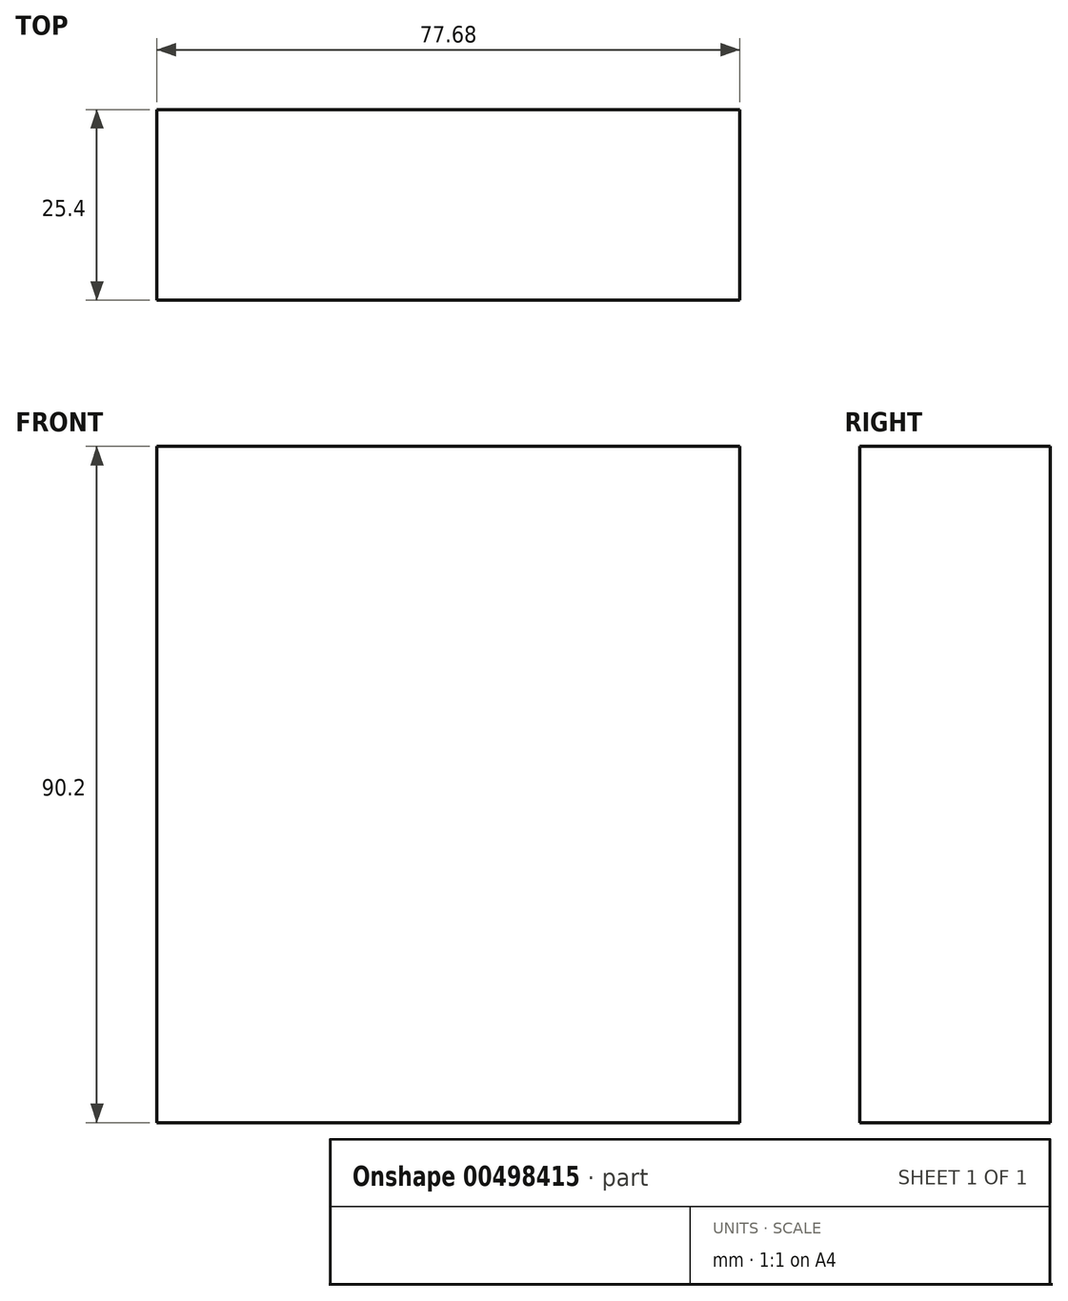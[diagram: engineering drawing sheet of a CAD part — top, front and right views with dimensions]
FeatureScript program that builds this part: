
annotation { "Feature Type Name" : "Feature", "Feature Type Description" : "" }
export const myFeature = defineFeature(function(context is Context, id is Id, definition is map)
    precondition{}
    {
        {
            var Q0;
            Q0=qCreatedBy(makeId("Front.planeOp"),FACE);
            var sketch = newSketch(context, id + "F0", { "sketchPlane" : qUnion([Q0])});
            skLineSegment(sketch, "E0.bottom", {"start": v(-33.07, 46.82) * mm, "end": v(44.61, 46.82) * mm});
            skLineSegment(sketch, "E0.top", {"start": v(-33.07, -43.38) * mm, "end": v(44.61, -43.38) * mm});
            skLineSegment(sketch, "E0.left", {"start": v(-33.07, 46.82) * mm, "end": v(-33.07, -43.38) * mm});
            skLineSegment(sketch, "E0.right", {"start": v(44.61, 46.82) * mm, "end": v(44.61, -43.38) * mm});
            skSolve(sketch);
        }
        {
            var Q0;
            Q0 = qSketchRegion(id + "F0", true);
            extrude(context, id + "F1", {"entities" : qUnion([Q0]), "depth" : 25.4 * mm});
        }
    });
